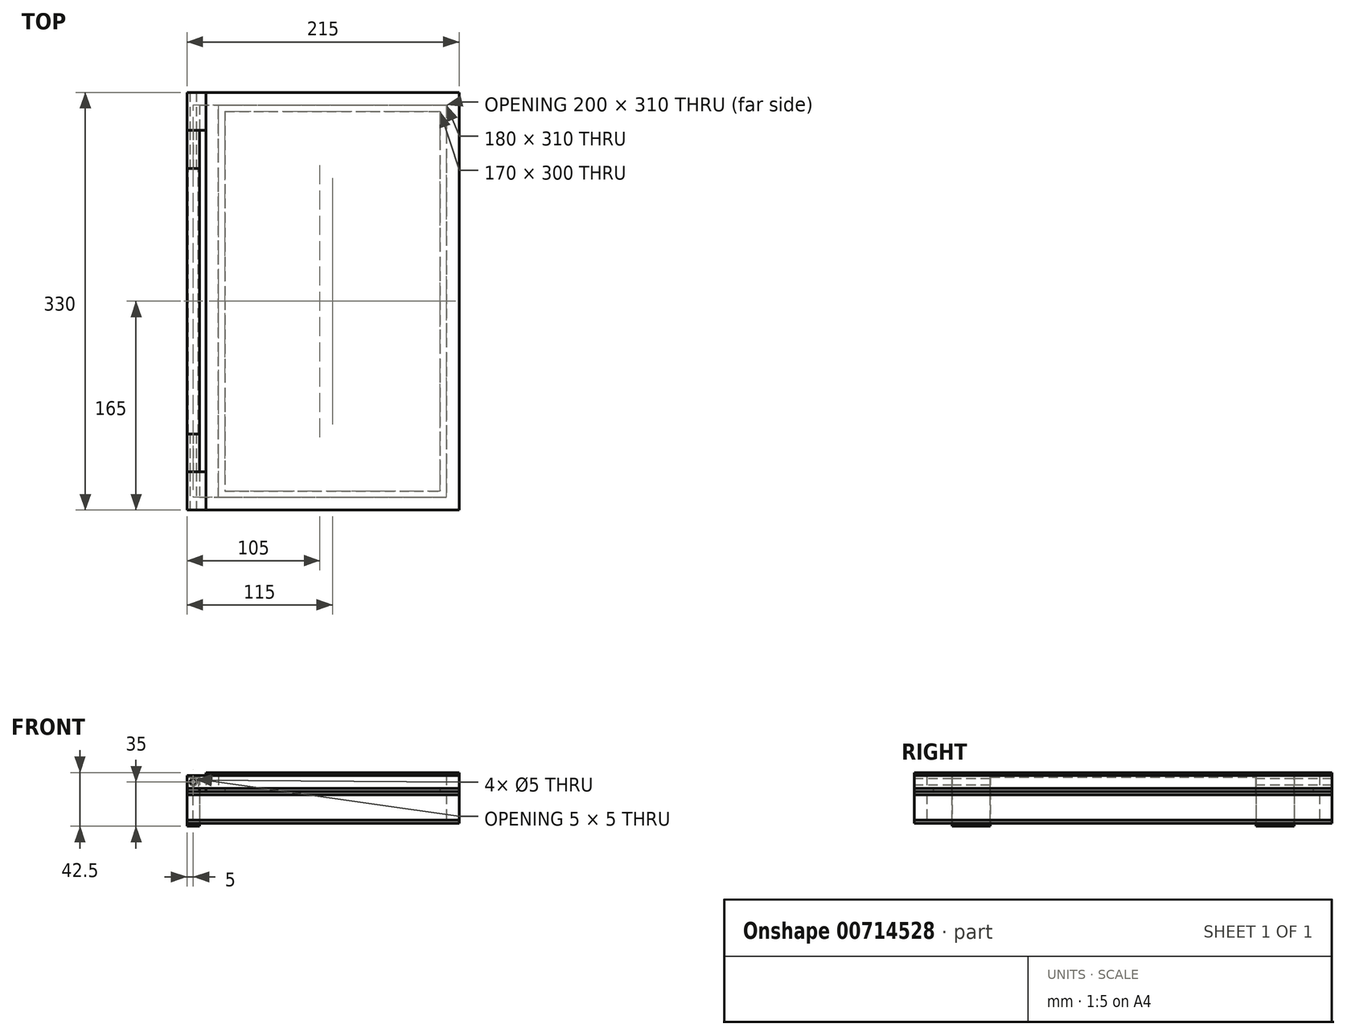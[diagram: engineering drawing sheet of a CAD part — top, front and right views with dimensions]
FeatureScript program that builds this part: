
annotation { "Feature Type Name" : "Feature", "Feature Type Description" : "" }
export const myFeature = defineFeature(function(context is Context, id is Id, definition is map)
    precondition{}
    {
        {
            var Q0;
            Q0=qCreatedBy(makeId("Top.planeOp"),FACE);
            var sketch = newSketch(context, id + "F0", { "sketchPlane" : qUnion([Q0])});
            skLineSegment(sketch, "E0.bottom", {"start": v(0, 0) * mm, "end": v(215, 0) * mm});
            skLineSegment(sketch, "E0.top", {"start": v(0, 330) * mm, "end": v(215, 330) * mm});
            skLineSegment(sketch, "E0.left", {"start": v(0, 0) * mm, "end": v(0, 330) * mm});
            skLineSegment(sketch, "E0.right", {"start": v(215, 0) * mm, "end": v(215, 330) * mm});
            skSolve(sketch);
        }
        {
            var Q0;
            Q0=makeQuery(id+"F0.imprint","IMPRINT",FACE,{"disambiguationData":[TD([[makeQuery(id+"F0.imprint","IMPRINT",EDGE,{"derivedFrom":sQuery(id+"F0.wireOp",EDGE,"E0.bottom")}),1.0]])]});
            extrude(context, id + "F1", {"entities" : qUnion([Q0]), "depth" : 2.5 * mm, "offsetDistance" : 25 * mm});
        }
        {
            var Q0;
            Q0=makeQuery(id+"F1.opExtrude","CAP_FACE",FACE,{"disambiguationData":[OSD([sQuery(id+"F0.wireOp",EDGE,"E0.bottom"),sQuery(id+"F0.wireOp",EDGE,"E0.top"),sQuery(id+"F0.wireOp",EDGE,"E0.left"),sQuery(id+"F0.wireOp",EDGE,"E0.right")])],"isStart":false});
            var sketch = newSketch(context, id + "F2", { "sketchPlane" : qUnion([Q0])});
            skLineSegment(sketch, "E1", {"start": v(215, 0) * mm, "end": v(215, 10) * mm, "construction": true});
            skLineSegment(sketch, "E2", {"start": v(215, 10) * mm, "end": v(205, 10) * mm, "construction": true});
            skLineSegment(sketch, "E3", {"start": v(0, 330) * mm, "end": v(0, 320) * mm, "construction": true});
            skLineSegment(sketch, "E4", {"start": v(0, 320) * mm, "end": v(10, 320) * mm, "construction": true});
            skLineSegment(sketch, "E5.bottom", {"start": v(10, 320) * mm, "end": v(205, 320) * mm});
            skLineSegment(sketch, "E5.top", {"start": v(10, 10) * mm, "end": v(205, 10) * mm});
            skLineSegment(sketch, "E5.left", {"start": v(10, 320) * mm, "end": v(10, 10) * mm});
            skLineSegment(sketch, "E5.right", {"start": v(205, 320) * mm, "end": v(205, 10) * mm});
            skLineSegment(sketch, "E6.bottom", {"start": v(0, 0) * mm, "end": v(215, 0) * mm});
            skLineSegment(sketch, "E6.top", {"start": v(0, 330) * mm, "end": v(215, 330) * mm});
            skLineSegment(sketch, "E6.left", {"start": v(0, 0) * mm, "end": v(0, 330) * mm});
            skLineSegment(sketch, "E6.right", {"start": v(215, 0) * mm, "end": v(215, 330) * mm});
            skSolve(sketch);
        }
        {
            var Q0;
            Q0 = qSketchRegion(id + "F2", true);
            extrude(context, id + "F3", {"entities" : qUnion([Q0]), "depth" : 20 * mm, "offsetDistance" : 25 * mm});
        }
        {
            var Q0;
            Q0=qCreatedBy(makeId("Front.planeOp"),FACE);
            var sketch = newSketch(context, id + "F4", { "sketchPlane" : qUnion([Q0])});
            skLineSegment(sketch, "E7", {"start": v(0, 0) * mm, "end": v(0, 2.5) * mm});
            skLineSegment(sketch, "E8", {"start": v(0, 2.5) * mm, "end": v(5, 2.5) * mm});
            skLineSegment(sketch, "E9", {"start": v(5, 2.5) * mm, "end": v(5, 22.5) * mm});
            skLineSegment(sketch, "E10", {"start": v(5, 22.5) * mm, "end": v(0, 22.5) * mm});
            skLineSegment(sketch, "E11", {"start": v(0, 22.5) * mm, "end": v(0, 37.5) * mm});
            skLineSegment(sketch, "E12", {"start": v(0, 37.5) * mm, "end": v(10, 37.5) * mm});
            skLineSegment(sketch, "E13", {"start": v(10, 37.5) * mm, "end": v(10, -2.5) * mm});
            skLineSegment(sketch, "E14", {"start": v(10, -2.5) * mm, "end": v(0, -2.5) * mm});
            skLineSegment(sketch, "E15", {"start": v(0, -2.5) * mm, "end": v(0, 0) * mm});
            skLineSegment(sketch, "E16", {"start": v(5, 37.5) * mm, "end": v(5, 32.5) * mm, "construction": true});
            skCircle(sketch, "E17", {"center": v(5, 32.5) * mm, "radius": 2.5 * mm});
            skSolve(sketch);
        }
        {
            var Q0;
            Q0 = qSketchRegion(id + "F4", true);
            extrude(context, id + "F5", {"entities" : qUnion([Q0]), "oppositeDirection" : true, "depth" : 30 * mm, "offsetDistance" : 25 * mm});
        }
        {
            var Q0;
            Q0=makeQuery(id+"F5.opExtrude","SWEPT_BODY",BODY,{"disambiguationData":[OSD([sQuery(id+"F4.wireOp",EDGE,"E7"),sQuery(id+"F4.wireOp",EDGE,"E8"),sQuery(id+"F4.wireOp",EDGE,"E9"),sQuery(id+"F4.wireOp",EDGE,"E10"),sQuery(id+"F4.wireOp",EDGE,"E11"),sQuery(id+"F4.wireOp",EDGE,"E12"),sQuery(id+"F4.wireOp",EDGE,"E13"),sQuery(id+"F4.wireOp",EDGE,"E14"),sQuery(id+"F4.wireOp",EDGE,"E15"),sQuery(id+"F4.wireOp",EDGE,"E17")])]});
            transform(context, id + "F6", {"entities" : qUnion([Q0]), "transformType" : TransformType.TRANSLATION_3D, "dx" : 0 * mm, "dy" : 30 * mm, "dz" : 0 * mm, "makeCopy" : false});
        }
        {
            var Q0;
            Q0=makeQuery(id+"F5.opExtrude","SWEPT_BODY",BODY,{"disambiguationData":[OSD([sQuery(id+"F4.wireOp",EDGE,"E7"),sQuery(id+"F4.wireOp",EDGE,"E8"),sQuery(id+"F4.wireOp",EDGE,"E9"),sQuery(id+"F4.wireOp",EDGE,"E10"),sQuery(id+"F4.wireOp",EDGE,"E11"),sQuery(id+"F4.wireOp",EDGE,"E12"),sQuery(id+"F4.wireOp",EDGE,"E13"),sQuery(id+"F4.wireOp",EDGE,"E14"),sQuery(id+"F4.wireOp",EDGE,"E15"),sQuery(id+"F4.wireOp",EDGE,"E17")])]});
            transform(context, id + "F7", {"entities" : qUnion([Q0]), "transformType" : TransformType.TRANSLATION_3D, "dx" : 0 * mm, "dy" : 240 * mm, "dz" : 0 * mm, "makeCopy" : true});
        }
        {
            var Q0;
            Q0=makeQuery(id+"F3.opExtrude","CAP_FACE",FACE,{"disambiguationData":[OSD([sQuery(id+"F2.wireOp",EDGE,"E5.bottom"),sQuery(id+"F2.wireOp",EDGE,"E5.top"),sQuery(id+"F2.wireOp",EDGE,"E5.left"),sQuery(id+"F2.wireOp",EDGE,"E5.right"),sQuery(id+"F2.wireOp",EDGE,"E6.bottom"),sQuery(id+"F2.wireOp",EDGE,"E6.top"),sQuery(id+"F2.wireOp",EDGE,"E6.left"),sQuery(id+"F2.wireOp",EDGE,"E6.right")])],"isStart":false});
            var sketch = newSketch(context, id + "F8", { "sketchPlane" : qUnion([Q0])});
            skLineSegment(sketch, "E18.bottom", {"start": v(0, 0) * mm, "end": v(215, 0) * mm});
            skLineSegment(sketch, "E18.top", {"start": v(0, 330) * mm, "end": v(215, 330) * mm});
            skLineSegment(sketch, "E18.left", {"start": v(0, 0) * mm, "end": v(0, 330) * mm});
            skLineSegment(sketch, "E18.right", {"start": v(215, 0) * mm, "end": v(215, 330) * mm});
            skSolve(sketch);
        }
        {
            var Q0;
            Q0 = qSketchRegion(id + "F8", true);
            extrude(context, id + "F9", {"entities" : qUnion([Q0]), "depth" : 2.5 * mm, "offsetDistance" : 25 * mm});
        }
        {
            var Q0;
            Q0=makeQuery(id+"F7.opPattern","COPY",BODY,{"derivedFrom":makeQuery(id+"F5.opExtrude","SWEPT_BODY",BODY,{"disambiguationData":[OSD([sQuery(id+"F4.wireOp",EDGE,"E7"),sQuery(id+"F4.wireOp",EDGE,"E8"),sQuery(id+"F4.wireOp",EDGE,"E9"),sQuery(id+"F4.wireOp",EDGE,"E10"),sQuery(id+"F4.wireOp",EDGE,"E11"),sQuery(id+"F4.wireOp",EDGE,"E12"),sQuery(id+"F4.wireOp",EDGE,"E13"),sQuery(id+"F4.wireOp",EDGE,"E14"),sQuery(id+"F4.wireOp",EDGE,"E15"),sQuery(id+"F4.wireOp",EDGE,"E17")])]}),"instanceName":"1"});
            var Q1;
            Q1=makeQuery(id+"F5.opExtrude","SWEPT_BODY",BODY,{"disambiguationData":[OSD([sQuery(id+"F4.wireOp",EDGE,"E7"),sQuery(id+"F4.wireOp",EDGE,"E8"),sQuery(id+"F4.wireOp",EDGE,"E9"),sQuery(id+"F4.wireOp",EDGE,"E10"),sQuery(id+"F4.wireOp",EDGE,"E11"),sQuery(id+"F4.wireOp",EDGE,"E12"),sQuery(id+"F4.wireOp",EDGE,"E13"),sQuery(id+"F4.wireOp",EDGE,"E14"),sQuery(id+"F4.wireOp",EDGE,"E15"),sQuery(id+"F4.wireOp",EDGE,"E17")])]});
            var Q2;
            Q2=makeQuery(id+"F3.opExtrude","SWEPT_BODY",BODY,{"disambiguationData":[OSD([sQuery(id+"F2.wireOp",EDGE,"E5.bottom"),sQuery(id+"F2.wireOp",EDGE,"E5.top"),sQuery(id+"F2.wireOp",EDGE,"E5.left"),sQuery(id+"F2.wireOp",EDGE,"E5.right"),sQuery(id+"F2.wireOp",EDGE,"E6.bottom"),sQuery(id+"F2.wireOp",EDGE,"E6.top"),sQuery(id+"F2.wireOp",EDGE,"E6.left"),sQuery(id+"F2.wireOp",EDGE,"E6.right")])]});
            var Q3;
            Q3=makeQuery(id+"F9.opExtrude","SWEPT_BODY",BODY,{"disambiguationData":[OSD([sQuery(id+"F8.wireOp",EDGE,"E18.bottom"),sQuery(id+"F8.wireOp",EDGE,"E18.top"),sQuery(id+"F8.wireOp",EDGE,"E18.left"),sQuery(id+"F8.wireOp",EDGE,"E18.right")])]});
            var Q4;
            Q4=makeQuery(id+"F1.opExtrude","SWEPT_BODY",BODY,{"disambiguationData":[OSD([sQuery(id+"F0.wireOp",EDGE,"E0.bottom"),sQuery(id+"F0.wireOp",EDGE,"E0.top"),sQuery(id+"F0.wireOp",EDGE,"E0.left"),sQuery(id+"F0.wireOp",EDGE,"E0.right")])]});
            booleanBodies(context, id + "F10", {"operationType" : BooleanOperationType.SUBTRACTION, "tools" : qUnion([Q0, Q1]), "targets" : qUnion([Q2, Q3, Q4]), "keepTools" : true});
        }
        {
            var Q0;
            Q0=makeQuery(id+"F9.opExtrude","CAP_FACE",FACE,{"disambiguationData":[OSD([sQuery(id+"F8.wireOp",EDGE,"E18.bottom"),sQuery(id+"F8.wireOp",EDGE,"E18.top"),sQuery(id+"F8.wireOp",EDGE,"E18.left"),sQuery(id+"F8.wireOp",EDGE,"E18.right")])],"isStart":false});
            var sketch = newSketch(context, id + "F11", { "sketchPlane" : qUnion([Q0])});
            skLineSegment(sketch, "E19.bottom", {"start": v(215, 0) * mm, "end": v(15, 0) * mm});
            skLineSegment(sketch, "E19.top", {"start": v(215, 330) * mm, "end": v(15, 330) * mm});
            skLineSegment(sketch, "E19.left", {"start": v(215, 0) * mm, "end": v(215, 330) * mm});
            skLineSegment(sketch, "E19.right", {"start": v(15, 0) * mm, "end": v(15, 330) * mm});
            skLineSegment(sketch, "E20", {"start": v(215, 0) * mm, "end": v(215, 15) * mm, "construction": true});
            skLineSegment(sketch, "E21", {"start": v(215, 15) * mm, "end": v(200, 15) * mm, "construction": true});
            skLineSegment(sketch, "E22", {"start": v(15, 330) * mm, "end": v(15, 315) * mm, "construction": true});
            skLineSegment(sketch, "E23", {"start": v(15, 315) * mm, "end": v(30, 315) * mm, "construction": true});
            skLineSegment(sketch, "E24.bottom", {"start": v(30, 315) * mm, "end": v(200, 315) * mm});
            skLineSegment(sketch, "E24.top", {"start": v(30, 15) * mm, "end": v(200, 15) * mm});
            skLineSegment(sketch, "E24.left", {"start": v(30, 315) * mm, "end": v(30, 15) * mm});
            skLineSegment(sketch, "E24.right", {"start": v(200, 315) * mm, "end": v(200, 15) * mm});
            skSolve(sketch);
        }
        {
            var Q0;
            Q0 = qSketchRegion(id + "F11", true);
            extrude(context, id + "F12", {"entities" : qUnion([Q0]), "depth" : 2.5 * mm, "offsetDistance" : 25 * mm});
        }
        {
            var Q0;
            Q0=makeQuery(id+"F12.opExtrude","CAP_FACE",FACE,{"disambiguationData":[OSD([sQuery(id+"F11.wireOp",EDGE,"E19.bottom"),sQuery(id+"F11.wireOp",EDGE,"E19.top"),sQuery(id+"F11.wireOp",EDGE,"E19.left"),sQuery(id+"F11.wireOp",EDGE,"E19.right"),sQuery(id+"F11.wireOp",EDGE,"E24.bottom"),sQuery(id+"F11.wireOp",EDGE,"E24.top"),sQuery(id+"F11.wireOp",EDGE,"E24.left"),sQuery(id+"F11.wireOp",EDGE,"E24.right")])],"isStart":false});
            var sketch = newSketch(context, id + "F13", { "sketchPlane" : qUnion([Q0])});
            skLineSegment(sketch, "E25.bottom", {"start": v(215, 0) * mm, "end": v(0, 0) * mm});
            skLineSegment(sketch, "E25.top", {"start": v(215, 330) * mm, "end": v(0, 330) * mm});
            skLineSegment(sketch, "E25.left", {"start": v(215, 0) * mm, "end": v(215, 330) * mm});
            skLineSegment(sketch, "E25.right", {"start": v(0, 0) * mm, "end": v(0, 330) * mm, "construction": true});
            skLineSegment(sketch, "E26", {"start": v(0, 0) * mm, "end": v(0, 30) * mm});
            skLineSegment(sketch, "E27", {"start": v(0, 30) * mm, "end": v(15, 30) * mm});
            skLineSegment(sketch, "E28", {"start": v(0, 330) * mm, "end": v(0, 300) * mm});
            skLineSegment(sketch, "E29", {"start": v(0, 300) * mm, "end": v(15, 300) * mm});
            skLineSegment(sketch, "E30", {"start": v(15, 300) * mm, "end": v(15, 30) * mm});
            skLineSegment(sketch, "E31", {"start": v(215, 330) * mm, "end": v(215, 320) * mm, "construction": true});
            skLineSegment(sketch, "E32", {"start": v(215, 320) * mm, "end": v(205, 320) * mm, "construction": true});
            skLineSegment(sketch, "E33", {"start": v(15, 30) * mm, "end": v(25, 30) * mm, "construction": true});
            skLineSegment(sketch, "E34", {"start": v(25, 30) * mm, "end": v(25, 10) * mm, "construction": true});
            skLineSegment(sketch, "E35.bottom", {"start": v(25, 10) * mm, "end": v(205, 10) * mm});
            skLineSegment(sketch, "E35.top", {"start": v(25, 320) * mm, "end": v(205, 320) * mm});
            skLineSegment(sketch, "E35.left", {"start": v(25, 10) * mm, "end": v(25, 320) * mm});
            skLineSegment(sketch, "E35.right", {"start": v(205, 10) * mm, "end": v(205, 320) * mm});
            skSolve(sketch);
        }
        {
            var Q0;
            Q0 = qSketchRegion(id + "F13", true);
            extrude(context, id + "F14", {"entities" : qUnion([Q0]), "depth" : 10 * mm, "offsetDistance" : 25 * mm});
        }
        {
            var Q0;
            Q0=makeQuery(id+"F14.opExtrude","CAP_FACE",FACE,{"disambiguationData":[OSD([sQuery(id+"F13.wireOp",EDGE,"E25.bottom"),sQuery(id+"F13.wireOp",EDGE,"E25.top"),sQuery(id+"F13.wireOp",EDGE,"E25.left"),sQuery(id+"F13.wireOp",EDGE,"E26"),sQuery(id+"F13.wireOp",EDGE,"E27"),sQuery(id+"F13.wireOp",EDGE,"E28"),sQuery(id+"F13.wireOp",EDGE,"E29"),sQuery(id+"F13.wireOp",EDGE,"E30"),sQuery(id+"F13.wireOp",EDGE,"E35.bottom"),sQuery(id+"F13.wireOp",EDGE,"E35.top"),sQuery(id+"F13.wireOp",EDGE,"E35.left"),sQuery(id+"F13.wireOp",EDGE,"E35.right")])],"isStart":false});
            var sketch = newSketch(context, id + "F15", { "sketchPlane" : qUnion([Q0])});
            skLineSegment(sketch, "E36.bottom", {"start": v(215, 0) * mm, "end": v(15, 0) * mm});
            skLineSegment(sketch, "E36.top", {"start": v(215, 330) * mm, "end": v(15, 330) * mm});
            skLineSegment(sketch, "E36.left", {"start": v(215, 0) * mm, "end": v(215, 330) * mm});
            skLineSegment(sketch, "E36.right", {"start": v(15, 0) * mm, "end": v(15, 330) * mm});
            skSolve(sketch);
        }
        {
            var Q0;
            Q0 = qSketchRegion(id + "F15", true);
            extrude(context, id + "F16", {"entities" : qUnion([Q0]), "depth" : 2.5 * mm, "offsetDistance" : 25 * mm});
        }
        {
            var Q0;
            Q0=makeQuery(id+"F14.opExtrude","SWEPT_FACE",FACE,{"disambiguationData":[OSD([sQuery(id+"F13.wireOp",EDGE,"E25.bottom")])]});
            var sketch = newSketch(context, id + "F17", { "sketchPlane" : qUnion([Q0])});
            skLineSegment(sketch, "E37", {"start": v(0, 32.5) * mm, "end": v(5, 32.5) * mm, "construction": true});
            skCircle(sketch, "E38", {"center": v(5, 32.5) * mm, "radius": 2.5 * mm});
            skSolve(sketch);
        }
        {
            var Q0;
            Q0 = qSketchRegion(id + "F17", true);
            extrude(context, id + "F18", {"entities" : qUnion([Q0]), "operationType" : NewBodyOperationType.REMOVE, "oppositeDirection" : true, "depth" : 999 * mm, "offsetDistance" : 25 * mm});
        }
        {
            var Q0;
            Q0=makeQuery(id+"F7.opPattern","COPY",FACE,{"derivedFrom":makeQuery(id+"F5.opExtrude","CAP_FACE",FACE,{"disambiguationData":[OSD([sQuery(id+"F4.wireOp",EDGE,"E7"),sQuery(id+"F4.wireOp",EDGE,"E8"),sQuery(id+"F4.wireOp",EDGE,"E9"),sQuery(id+"F4.wireOp",EDGE,"E10"),sQuery(id+"F4.wireOp",EDGE,"E11"),sQuery(id+"F4.wireOp",EDGE,"E12"),sQuery(id+"F4.wireOp",EDGE,"E13"),sQuery(id+"F4.wireOp",EDGE,"E14"),sQuery(id+"F4.wireOp",EDGE,"E15"),sQuery(id+"F4.wireOp",EDGE,"E17")])],"isStart":true}),"instanceName":"1"});
            var sketch = newSketch(context, id + "F19", { "sketchPlane" : qUnion([Q0])});
            skLineSegment(sketch, "E39", {"start": v(0, 37.5) * mm, "end": v(0, 25) * mm});
            skLineSegment(sketch, "E40", {"start": v(0, 25) * mm, "end": v(1, 25) * mm});
            skLineSegment(sketch, "E41", {"start": v(1, 25) * mm, "end": v(1, 36.5) * mm});
            skLineSegment(sketch, "E42", {"start": v(1, 36.5) * mm, "end": v(9, 36.5) * mm});
            skLineSegment(sketch, "E43", {"start": v(9, 36.5) * mm, "end": v(9, 25) * mm});
            skLineSegment(sketch, "E44", {"start": v(9, 25) * mm, "end": v(10, 25) * mm});
            skLineSegment(sketch, "E45", {"start": v(10, 25) * mm, "end": v(10, 37.5) * mm});
            skLineSegment(sketch, "E46", {"start": v(10, 37.5) * mm, "end": v(0, 37.5) * mm});
            skSolve(sketch);
        }
        {
            var Q0;
            Q0 = qSketchRegion(id + "F19", true);
            extrude(context, id + "F20", {"entities" : qUnion([Q0]), "endBound" : BoundingType.UP_TO_NEXT, "depth" : 25 * mm, "offsetDistance" : 25 * mm});
        }
    });
